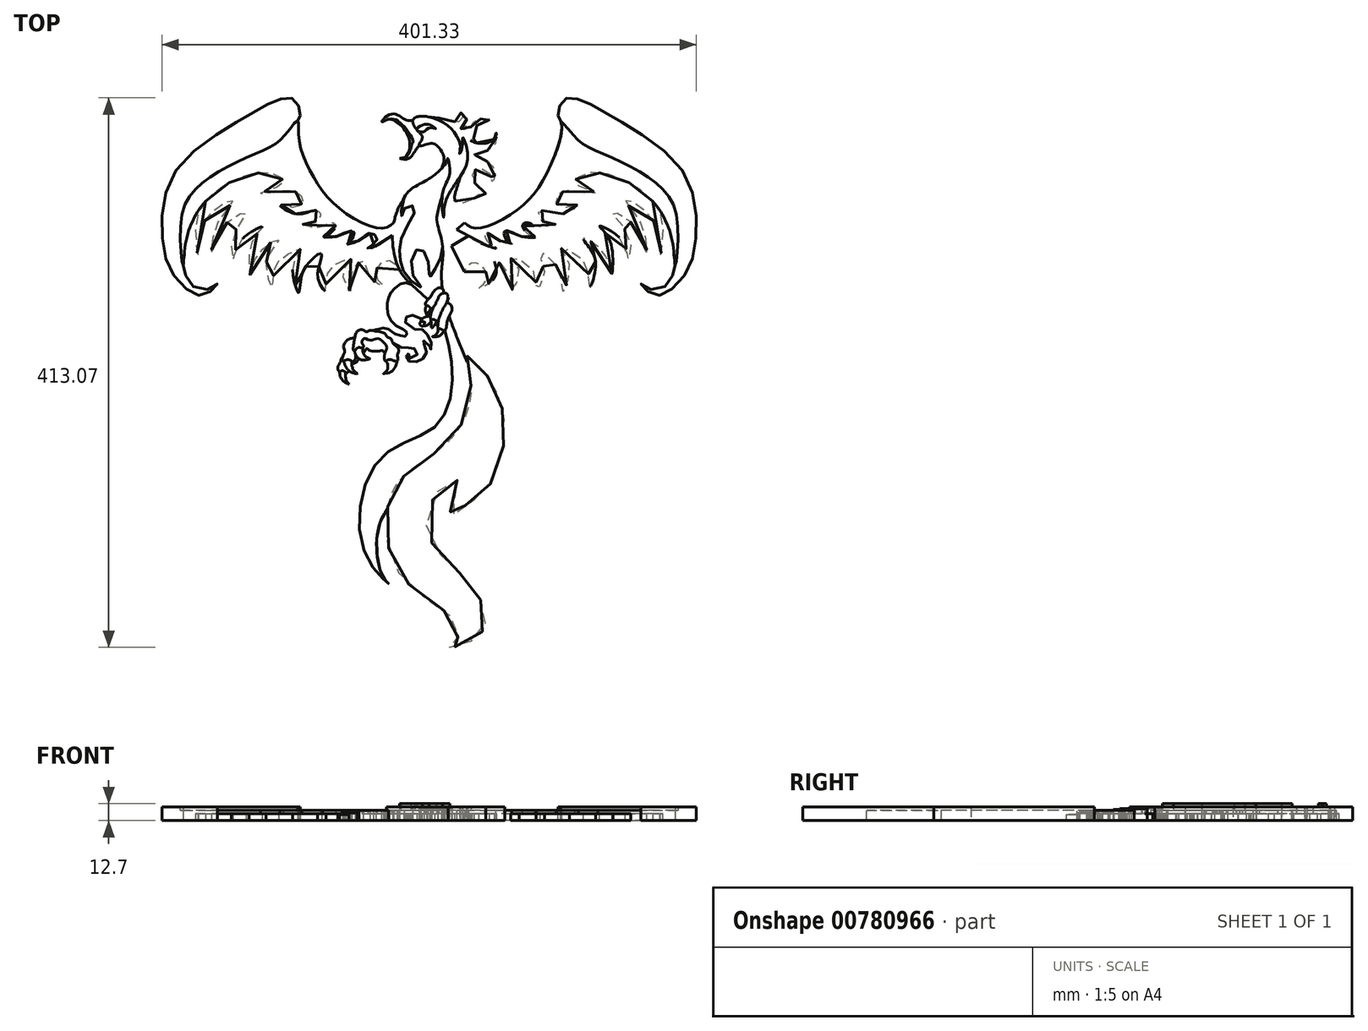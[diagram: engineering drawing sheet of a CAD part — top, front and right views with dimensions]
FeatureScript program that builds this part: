
annotation { "Feature Type Name" : "Feature", "Feature Type Description" : "" }
export const myFeature = defineFeature(function(context is Context, id is Id, definition is map)
    precondition{}
    {
        {
            var Q0;
            Q0=qCreatedBy(makeId("Top.planeOp"),FACE);
            var sketch = newSketch(context, id + "F0", { "sketchPlane" : qUnion([Q0])});
            skFitSpline(sketch, "E0", {"points": [v(-8.67, -5.4) * mm, v(-1.51, -5.23) * mm, v(5.92, 4.18) * mm], "startDerivative": vector(15.7, -3.66) * mm, "endDerivative": vector(12.22, 12.43) * mm});
            skFitSpline(sketch, "E1", {"points": [v(-8.67, -5.4) * mm, v(-2.53, -3.06) * mm, v(0.73, 5.89) * mm, v(1.36, 7.8) * mm, v(-8.37, 21.6) * mm, v(-17.76, 23.8) * mm, v(-21.93, 22.06) * mm, v(-17.64, 26.92) * mm, v(-9.88, 27.16) * mm, v(-3.62, 23.33) * mm, v(1.2, 23.22) * mm], "startDerivative": vector(82.86, 14.8) * mm, "endDerivative": vector(29.37, 4.58) * mm});
            skFitSpline(sketch, "E2", {"points": [v(1.2, 23.22) * mm, v(2.12, 19.15) * mm, v(7.1, 12.99) * mm, v(8.33, 9.8) * mm, v(5.92, 4.18) * mm], "startDerivative": vector(-2.31, -12.7) * mm, "endDerivative": vector(8.26, -4.5) * mm});
            skFitSpline(sketch, "E3", {"points": [v(5.92, 4.18) * mm, v(10.45, 4.85) * mm, v(16.15, 5.81) * mm, v(20.15, 3.52) * mm, v(24.67, -6.53) * mm, v(22.82, -13.16) * mm, v(26.33, -8) * mm, v(27.43, -5.42) * mm, v(28.96, -12.46) * mm, v(28.03, -20.36) * mm, v(23.4, -32.68) * mm, v(24.32, -49.78) * mm, v(25.42, -39.7) * mm, v(36.84, -18.84) * mm, v(42.4, -2.62) * mm, v(38.88, 10.39) * mm, v(38.42, 3.1) * mm, v(36.33, -2.1) * mm, v(36.95, 3.26) * mm, v(32.84, 13.56) * mm, v(26.03, 20.48) * mm, v(12.13, 26.04) * mm, v(3, 25.35) * mm, v(1.2, 23.22) * mm], "startDerivative": vector(43.44, -38.23) * mm, "endDerivative": vector(-67.27, -103.93) * mm});
            skFitSpline(sketch, "E4", {"points": [v(12.13, 26.04) * mm, v(15.22, 26.19) * mm, v(18.86, 25.62) * mm, v(27.7, 22.76) * mm, v(33.96, 22.28) * mm, v(38.93, 24.76) * mm, v(36.9, 29.97) * mm, v(39.54, 27.16) * mm, v(41.95, 23.13) * mm, v(39.78, 17.7) * mm, v(37.35, 16.77) * mm, v(41.25, 16.3) * mm, v(44.74, 17.94) * mm, v(46.59, 21.82) * mm, v(51.24, 24.3) * mm, v(57.52, 23.6) * mm, v(59.02, 24.23) * mm, v(56.82, 22.27) * mm, v(51.47, 21.43) * mm, v(48.3, 16.62) * mm, v(47.68, 11.2) * mm, v(45.76, 8.24) * mm, v(44.62, 8.18) * mm, v(47.37, 6.77) * mm, v(56.63, 6.21) * mm, v(62.77, 10.38) * mm, v(63.86, 13.8) * mm, v(63.97, 8.3) * mm, v(60.46, 2.6) * mm, v(52.02, -1.13) * mm, v(47.62, -2) * mm, v(49.17, -4.1) * mm, v(56.29, -7.21) * mm, v(62.38, -13.48) * mm, v(62.38, -20.12) * mm, v(61, -23.18) * mm, v(59.48, -17.45) * mm, v(49.83, -13.4) * mm, v(45.95, -16.8) * mm, v(47.8, -23.81) * mm, v(52.8, -28.94) * mm, v(56.06, -32.14) * mm, v(52.13, -32.13) * mm, v(43.68, -37.59) * mm, v(32.95, -37.47) * mm, v(36.84, -18.84) * mm], "startDerivative": vector(205.97, 15.52) * mm, "endDerivative": vector(10.23, 256.7) * mm});
            skFitSpline(sketch, "E5", {"points": [v(22.82, -13.16) * mm, v(11.24, -22.05) * mm, v(-5.1, -34.67) * mm, v(-7.41, -48.86) * mm, v(-4.2, -41.9) * mm, v(2.54, -42.64) * mm, v(-6.53, -63.03) * mm, v(-8.4, -80.24) * mm, v(-2.77, -94.45) * mm, v(8.3, -102.75) * mm, v(0.37, -90.76) * mm, v(5.71, -73.25) * mm, v(13.09, -83.94) * mm, v(13.64, -94.45) * mm, v(18.06, -88.18) * mm, v(23.52, -71.72) * mm, v(19.43, -52.46) * mm, v(20.97, -41.44) * mm, v(23.4, -32.68) * mm], "startDerivative": vector(-178.8, -166.71) * mm, "endDerivative": vector(68.52, 243.93) * mm});
            skFitSpline(sketch, "E6", {"points": [v(36.84, -18.84) * mm, v(32.95, -37.47) * mm, v(43.41, -66.2) * mm, v(33.77, -122.4) * mm, v(49.97, -143.97) * mm, v(89.81, -174.41) * mm, v(99.05, -195) * mm, v(91.6, -185.33) * mm, v(69.37, -169.92) * mm, v(96.61, -209.66) * mm, v(65.57, -275.96) * mm, v(59.93, -314.37) * mm, v(73.97, -336.1) * mm, v(54.52, -318.94) * mm, v(41.72, -279.7) * mm, v(61.44, -227.4) * mm, v(47.15, -170.24) * mm, v(23.12, -99.01) * mm], "startDerivative": vector(-182.42, -334.69) * mm, "endDerivative": vector(10.33, 536.26) * mm});
            skFitSpline(sketch, "E7", {"points": [v(-5.1, -34.67) * mm, v(-10.55, -45) * mm, v(-13.94, -60.48) * mm, v(-11.55, -82.2) * mm, v(-3.83, -96.22) * mm, v(10.63, -109.72) * mm, v(20.2, -122.95) * mm, v(30.07, -156.04) * mm, v(20.34, -204.72) * mm, v(-23.05, -230.83) * mm, v(-34.59, -302.46) * mm, v(-17.09, -324.94) * mm, v(-21.5, -318.95) * mm, v(-23.29, -278.8) * mm, v(0, -254.64) * mm, v(24.7, -238.54) * mm, v(40.92, -217.08) * mm, v(47.15, -170.24) * mm, v(23.12, -99.01) * mm, v(23.52, -71.72) * mm], "startDerivative": vector(-275.41, -490.32) * mm, "endDerivative": vector(-88.37, 555.9) * mm});
            skFitSpline(sketch, "E8", {"points": [v(-16.35, 24.17) * mm, v(-13.7, 23.48) * mm, v(-6.2, 17.76) * mm, v(-2.4, 11.42) * mm, v(-1.24, 7.43) * mm, v(-1.17, 2.67) * mm, v(-4.02, -4.31) * mm], "startDerivative": vector(25.5, -4.77) * mm, "endDerivative": vector(-29.98, -38.45) * mm});
            skSolve(sketch);
        }
        {
            var Q0;
            {var subQ2=sQuery(id+"F0.wireOp",EDGE,"E7");Q0=makeQuery(id+"F0.imprint","IMPRINT",FACE,{"disambiguationData":[TD([[makeQuery(id+"F0.imprint","IMPRINT",EDGE,{"derivedFrom":subQ2}),1.0]])]});}
            extrude(context, id + "F1", {"entities" : qUnion([Q0]), "depth" : 7.62 * mm, "offsetDistance" : 25.4 * mm});
        }
        {
            var Q0;
            {var subQ5=sQuery(id+"F0.wireOp",EDGE,"E2");Q0=makeQuery(id+"F0.imprint","IMPRINT",FACE,{"disambiguationData":[TD([[makeQuery(id+"F0.imprint","IMPRINT",EDGE,{"derivedFrom":subQ5}),1.0]])]});}
            extrude(context, id + "F2", {"entities" : qUnion([Q0]), "operationType" : NewBodyOperationType.ADD, "depth" : 10.16 * mm, "offsetDistance" : 25.4 * mm});
        }
        {
            var Q0;
            {var subQ0=sQuery(id+"F0.wireOp",EDGE,"E5");var subQ1=sQuery(id+"F0.wireOp",EDGE,"E3");var subQ2=makeQuery(id+"F0.imprint","INTERSECT",VERTEX,{"disambiguationData":[OD(0.0)],"derivedFrom":[subQ1,subQ0]});Q0=makeQuery(id+"F0.imprint","IMPRINT",FACE,{"disambiguationData":[TD([[makeQuery(id+"F0.imprint","IMPRINT",EDGE,{"disambiguationData":[TD([[subQ2,-1.0]])],"derivedFrom":subQ1}),-1.0]])]});}
            extrude(context, id + "F3", {"entities" : qUnion([Q0]), "operationType" : NewBodyOperationType.ADD, "depth" : 12.7 * mm, "offsetDistance" : 25.4 * mm});
        }
        {
            var Q0;
            {var subQ0=sQuery(id+"F0.wireOp",EDGE,"E4");Q0=makeQuery(id+"F0.imprint","IMPRINT",FACE,{"disambiguationData":[TD([[makeQuery(id+"F0.imprint","IMPRINT",EDGE,{"derivedFrom":subQ0}),-1.0]])]});}
            extrude(context, id + "F4", {"entities" : qUnion([Q0]), "operationType" : NewBodyOperationType.ADD, "depth" : 5.08 * mm, "offsetDistance" : 25.4 * mm});
        }
        {
            var Q0;
            Q0=makeQuery(id+"F0.imprint","IMPRINT",FACE,{"disambiguationData":[TD([[makeQuery(id+"F0.imprint","IMPRINT",EDGE,{"derivedFrom":sQuery(id+"F0.wireOp",EDGE,"E0")}),1.0]])]});
            extrude(context, id + "F5", {"entities" : qUnion([Q0]), "operationType" : NewBodyOperationType.ADD, "depth" : 7.62 * mm, "offsetDistance" : 25.4 * mm});
        }
        {
            var Q0;
            {var subQ0=sQuery(id+"F0.wireOp",EDGE,"E8");Q0=makeQuery(id+"F0.imprint","IMPRINT",FACE,{"disambiguationData":[TD([[makeQuery(id+"F0.imprint","IMPRINT",EDGE,{"derivedFrom":subQ0}),1.0]])]});}
            extrude(context, id + "F6", {"entities" : qUnion([Q0]), "operationType" : NewBodyOperationType.ADD, "depth" : 5.08 * mm, "offsetDistance" : 25.4 * mm});
        }
        {
            var Q0;
            Q0=qCreatedBy(makeId("Top.planeOp"),FACE);
            var sketch = newSketch(context, id + "F7", { "sketchPlane" : qUnion([Q0])});
            skFitSpline(sketch, "E9", {"points": [v(-0.05, -100.04) * mm, v(-7, -99.44) * mm, v(-15.14, -106.14) * mm, v(-17.67, -112.32) * mm, v(-17.85, -120.4) * mm, v(-12.81, -129.85) * mm, v(-4, -135.24) * mm, v(-3.6, -136.14) * mm, v(-3.7, -138.8) * mm, v(-7, -138.9) * mm, v(-13.37, -136.6) * mm, v(-15.47, -134.55) * mm, v(-22.15, -132.9) * mm, v(-23.45, -133.48) * mm, v(-24.06, -133.81) * mm, v(-24.8, -133.81) * mm, v(-27.03, -134.13) * mm, v(-28.4, -134.86) * mm, v(-25.76, -135.3) * mm, v(-19.62, -137.13) * mm, v(-18.12, -139.43) * mm, v(-15.05, -141.02) * mm, v(-13.85, -143.78) * mm, v(-4.3, -147.98) * mm, v(-1.16, -147.63) * mm, v(3.71, -149.11) * mm, v(3.4, -154.42) * mm, v(-2.96, -154.63) * mm, v(-1.88, -151.62) * mm, v(-4.02, -154.84) * mm, v(-0.49, -158.24) * mm, v(5.25, -157.93) * mm, v(9.91, -154.71) * mm, v(11.49, -148.47) * mm, v(8.27, -142.42) * mm, v(13.31, -145) * mm, v(14.62, -149.47) * mm, v(15.27, -146.9) * mm, v(14.15, -141.1) * mm, v(8.44, -133.89) * mm, v(5.23, -134.6) * mm, v(-5.18, -127.03) * mm, v(-2.66, -124.12) * mm, v(2.14, -123.44) * mm, v(14.91, -129.74) * mm, v(20.87, -129.74) * mm, v(23.08, -129.18) * mm], "startDerivative": vector(-259.15, 144.37) * mm, "endDerivative": vector(81.22, 23.95) * mm});
            skFitSpline(sketch, "E10", {"points": [v(-28.4, -134.86) * mm, v(-29.8, -134.86) * mm, v(-31.04, -134.63) * mm, v(-33.06, -135.6) * mm, v(-36.37, -134.38) * mm, v(-40.34, -135.1) * mm, v(-42.2, -139.48) * mm, v(-43.05, -143.55) * mm, v(-43.4, -146.9) * mm, v(-43.6, -148.85) * mm, v(-42.73, -150.17) * mm, v(-40, -147.63) * mm, v(-36.53, -147.75) * mm, v(-35.76, -146.13) * mm, v(-36.92, -144.07) * mm, v(-35.42, -140.74) * mm, v(-30.25, -142.24) * mm, v(-25.82, -140.8) * mm, v(-20.08, -144.12) * mm, v(-18.28, -148.03) * mm, v(-20.02, -152.96) * mm, v(-19.4, -157.7) * mm, v(-17.45, -156.72) * mm, v(-14.15, -156.98) * mm, v(-10.5, -157.7) * mm, v(-9.9, -155.4) * mm, v(-10.28, -152.79) * mm, v(-9.3, -149.86) * mm, v(-10.05, -147.7) * mm, v(-11.29, -146.54) * mm, v(-12.24, -145.65) * mm, v(-13.85, -143.78) * mm], "startDerivative": vector(-126.28, 25.7) * mm, "endDerivative": vector(-46.26, 137.95) * mm});
            skFitSpline(sketch, "E11", {"points": [v(-42.2, -139.48) * mm, v(-45.85, -140.83) * mm, v(-48.34, -142.22) * mm, v(-50.14, -144.52) * mm, v(-50.85, -147.35) * mm, v(-49.91, -150.65) * mm, v(-50.5, -152.34) * mm, v(-51.66, -155.06) * mm, v(-51.3, -157.56) * mm, v(-48.67, -156.8) * mm, v(-45.55, -157.16) * mm, v(-44.27, -158.06) * mm, v(-42.54, -157.28) * mm, v(-41.75, -154.38) * mm, v(-41.87, -152.53) * mm], "startDerivative": vector(-26.53, -31.12) * mm, "endDerivative": vector(-3.12, 47.85) * mm});
            skFitSpline(sketch, "E12", {"points": [v(-19.4, -157.7) * mm, v(-18.01, -159.15) * mm, v(-17.67, -162.54) * mm, v(-18.37, -165.08) * mm, v(-20.85, -167.18) * mm, v(-18.45, -166.8) * mm, v(-15, -165.68) * mm, v(-12, -162.16) * mm, v(-11.03, -159.08) * mm, v(-10.5, -157.7) * mm], "startDerivative": vector(17.76, -12.44) * mm, "endDerivative": vector(6.99, 15.7) * mm});
            skFitSpline(sketch, "E13", {"points": [v(-42.73, -150.17) * mm, v(-41.87, -152.53) * mm, v(-39.64, -155.63) * mm, v(-36.35, -156.92) * mm, v(-32.38, -156.48) * mm, v(-31.05, -155.87) * mm, v(-32.09, -155.45) * mm, v(-34.15, -154.43) * mm, v(-35.7, -152.12) * mm, v(-36.34, -150.17) * mm, v(-36.53, -147.75) * mm], "startDerivative": vector(15.67, -24.18) * mm, "endDerivative": vector(-3.95, 15.32) * mm});
            skFitSpline(sketch, "E14", {"points": [v(-51.3, -157.56) * mm, v(-50.16, -159.43) * mm, v(-49.26, -161.63) * mm, v(-48.22, -163.28) * mm, v(-46.96, -164.92) * mm, v(-45.42, -165.93) * mm, v(-42.58, -166.92) * mm, v(-40.6, -167.2) * mm, v(-42.51, -165.5) * mm, v(-44, -163.01) * mm, v(-44.68, -159.78) * mm, v(-44.27, -158.06) * mm], "startDerivative": vector(27.67, -20.95) * mm, "endDerivative": vector(13.92, 15.87) * mm});
            skFitSpline(sketch, "E15", {"points": [v(-51.66, -155.06) * mm, v(-52.8, -157.14) * mm, v(-54.13, -160.22) * mm, v(-55.19, -162.65) * mm, v(-54.6, -164.83) * mm, v(-53.92, -165.57) * mm, v(-52.22, -165.04) * mm, v(-50.2, -165.46) * mm, v(-48.99, -166.47) * mm, v(-47.88, -166.36) * mm, v(-46.96, -164.92) * mm], "startDerivative": vector(-25.42, -13.3) * mm, "endDerivative": vector(3.8, 21.11) * mm});
            skFitSpline(sketch, "E16", {"points": [v(-53.92, -165.57) * mm, v(-53.65, -167.48) * mm, v(-53.33, -169.28) * mm, v(-52.38, -171.03) * mm, v(-51, -172.57) * mm, v(-48.78, -174.2) * mm, v(-46.88, -175) * mm, v(-48.09, -173.41) * mm, v(-48.99, -171.45) * mm, v(-49.3, -169.33) * mm, v(-49.3, -167.58) * mm, v(-48.99, -166.47) * mm], "startDerivative": vector(7.77, -26.41) * mm, "endDerivative": vector(13.13, 12.03) * mm});
            skFitSpline(sketch, "E17", {"points": [v(-44.68, -159.78) * mm, v(-43.41, -159.53) * mm, v(-42.06, -159.18) * mm, v(-40.86, -158.2) * mm, v(-40.01, -156.9) * mm, v(-40.1, -155.2) * mm], "startDerivative": vector(13.67, 4.14) * mm, "endDerivative": vector(0.69, 4.69) * mm});
            skFitSpline(sketch, "E18", {"points": [v(-35.98, -151.52) * mm, v(-34.9, -150.38) * mm, v(-33.29, -148.2) * mm, v(-32.1, -149.37) * mm, v(-28.9, -150.26) * mm, v(-26.32, -150.41) * mm, v(-23.49, -150.04) * mm, v(-21.6, -149.76) * mm, v(-20.69, -150.68) * mm, v(-19.73, -151.92) * mm], "startDerivative": vector(8.82, 8.41) * mm, "endDerivative": vector(10.7, -12.63) * mm});
            skLineSegment(sketch, "E19", {"start": v(-0.05, -100.04) * mm, "end": v(28.04, -110.01) * mm});
            skLineSegment(sketch, "E20", {"start": v(28.04, -110.01) * mm, "end": v(23.08, -129.18) * mm});
            skSolve(sketch);
        }
        {
            var Q0;
            {var subQ0=sQuery(id+"F7.wireOp",EDGE,"E19");Q0=makeQuery(id+"F7.imprint","IMPRINT",FACE,{"disambiguationData":[TD([[makeQuery(id+"F7.imprint","IMPRINT",EDGE,{"derivedFrom":subQ0}),-1.0]])]});}
            extrude(context, id + "F8", {"entities" : qUnion([Q0]), "operationType" : NewBodyOperationType.ADD, "depth" : 5.08 * mm, "offsetDistance" : 25.4 * mm});
        }
        {
            var Q0;
            {var subQ1=sQuery(id+"F7.wireOp",EDGE,"E10");var subQ5=sQuery(id+"F7.wireOp",EDGE,"E9");var subQ6=makeQuery(id+"F7.imprint","INTERSECT",VERTEX,{"disambiguationData":[OD(0.0)],"derivedFrom":[subQ5,subQ1]});Q0=makeQuery(id+"F7.imprint","IMPRINT",FACE,{"disambiguationData":[TD([[makeQuery(id+"F7.imprint","IMPRINT",EDGE,{"disambiguationData":[TD([[subQ6,-1.0]])],"derivedFrom":subQ5}),-1.0]])]});}
            extrude(context, id + "F9", {"entities" : qUnion([Q0]), "operationType" : NewBodyOperationType.ADD, "depth" : 7.62 * mm, "offsetDistance" : 25.4 * mm});
        }
        {
            var Q0;
            {var subQ1=sQuery(id+"F7.wireOp",EDGE,"E11");var subQ5=sQuery(id+"F7.wireOp",EDGE,"E10");var subQ6=makeQuery(id+"F7.imprint","INTERSECT",VERTEX,{"derivedFrom":[subQ5,subQ1]});Q0=makeQuery(id+"F7.imprint","IMPRINT",FACE,{"disambiguationData":[TD([[makeQuery(id+"F7.imprint","IMPRINT",EDGE,{"disambiguationData":[TD([[subQ6,-1.0]])],"derivedFrom":subQ5}),-1.0]])]});}
            extrude(context, id + "F10", {"entities" : qUnion([Q0]), "operationType" : NewBodyOperationType.ADD, "depth" : 6.35 * mm, "offsetDistance" : 25.4 * mm});
        }
        {
            var Q0;
            {var subQ3=sQuery(id+"F7.wireOp",EDGE,"E18");Q0=makeQuery(id+"F7.imprint","IMPRINT",FACE,{"disambiguationData":[TD([[makeQuery(id+"F7.imprint","IMPRINT",EDGE,{"derivedFrom":subQ3}),1.0]])]});}
            var Q1;
            {var subQ5=sQuery(id+"F7.wireOp",EDGE,"E17");Q1=makeQuery(id+"F7.imprint","IMPRINT",FACE,{"disambiguationData":[TD([[makeQuery(id+"F7.imprint","IMPRINT",EDGE,{"derivedFrom":subQ5}),1.0]])]});}
            var Q2;
            {var subQ4=sQuery(id+"F7.wireOp",EDGE,"E11");var subQ6=sQuery(id+"F7.wireOp",EDGE,"E14");var subQ7=makeQuery(id+"F7.imprint","INTERSECT",VERTEX,{"disambiguationData":[OD(0.0)],"derivedFrom":[subQ4,subQ6]});Q2=makeQuery(id+"F7.imprint","IMPRINT",FACE,{"disambiguationData":[TD([[makeQuery(id+"F7.imprint","IMPRINT",EDGE,{"disambiguationData":[TD([[subQ7,1.0]])],"derivedFrom":subQ4}),-1.0]])]});}
            extrude(context, id + "F11", {"entities" : qUnion([Q0, Q1, Q2]), "operationType" : NewBodyOperationType.ADD, "depth" : 5.08 * mm, "offsetDistance" : 25.4 * mm});
        }
        {
            var Q0;
            {var subQ0=sQuery(id+"F7.wireOp",EDGE,"E16");Q0=makeQuery(id+"F7.imprint","IMPRINT",FACE,{"disambiguationData":[TD([[makeQuery(id+"F7.imprint","IMPRINT",EDGE,{"derivedFrom":subQ0}),1.0]])]});}
            extrude(context, id + "F12", {"entities" : qUnion([Q0]), "operationType" : NewBodyOperationType.ADD, "depth" : 4.44 * mm, "offsetDistance" : 25.4 * mm});
        }
        {
            var Q0;
            {var subQ0=sQuery(id+"F7.wireOp",EDGE,"E14");var subQ1=sQuery(id+"F7.wireOp",EDGE,"E11");var subQ2=makeQuery(id+"F7.imprint","INTERSECT",VERTEX,{"disambiguationData":[OD(0.0)],"derivedFrom":[subQ1,subQ0]});Q0=makeQuery(id+"F7.imprint","IMPRINT",FACE,{"disambiguationData":[TD([[makeQuery(id+"F7.imprint","IMPRINT",EDGE,{"disambiguationData":[TD([[subQ2,-1.0]])],"derivedFrom":subQ1}),-1.0]])]});}
            extrude(context, id + "F13", {"entities" : qUnion([Q0]), "operationType" : NewBodyOperationType.ADD, "depth" : 5.7 * mm, "offsetDistance" : 25.4 * mm});
        }
        {
            var Q0;
            {var subQ0=sQuery(id+"F7.wireOp",EDGE,"E13");var subQ4=sQuery(id+"F7.wireOp",EDGE,"E10");var subQ5=makeQuery(id+"F7.imprint","INTERSECT",VERTEX,{"disambiguationData":[OD(0.0)],"derivedFrom":[subQ4,subQ0]});Q0=makeQuery(id+"F7.imprint","IMPRINT",FACE,{"disambiguationData":[TD([[makeQuery(id+"F7.imprint","IMPRINT",EDGE,{"disambiguationData":[TD([[subQ5,-1.0]])],"derivedFrom":subQ4}),-1.0]])]});}
            var Q1;
            {var subQ0=sQuery(id+"F7.wireOp",EDGE,"E12");Q1=makeQuery(id+"F7.imprint","IMPRINT",FACE,{"disambiguationData":[TD([[makeQuery(id+"F7.imprint","IMPRINT",EDGE,{"derivedFrom":subQ0}),1.0]])]});}
            extrude(context, id + "F14", {"entities" : qUnion([Q0, Q1]), "operationType" : NewBodyOperationType.ADD, "depth" : 7 * mm, "offsetDistance" : 25.4 * mm});
        }
        {
            var Q0;
            Q0=qCreatedBy(makeId("Top.planeOp"),FACE);
            var sketch = newSketch(context, id + "F15", { "sketchPlane" : qUnion([Q0])});
            skFitSpline(sketch, "E21", {"points": [v(40.02, -53.8) * mm, v(48.94, -57.92) * mm, v(78.57, -44.94) * mm, v(101.16, -17.9) * mm, v(113.1, 18.52) * mm, v(112.35, 22.9) * mm, v(121.04, 13) * mm, v(131.84, 3.6) * mm, v(155.22, -6.78) * mm, v(185.2, -25.07) * mm, v(199.9, -52.06) * mm, v(198.4, -85.64) * mm, v(196.3, -68.55) * mm, v(181.6, -37.67) * mm, v(157.59, -20.7) * mm, v(131.02, -16.77) * mm, v(123.6, -24.26) * mm, v(140.03, -31.4) * mm, v(127.9, -30.32) * mm, v(114.08, -30.32) * mm, v(108.54, -35.67) * mm, v(112.93, -42.12) * mm, v(125.48, -40.4) * mm, v(113.77, -47.08) * mm, v(98.99, -44.59) * mm, v(95, -47.44) * mm, v(101.79, -54.1) * mm, v(109.2, -54.41) * mm, v(97.44, -57.17) * mm, v(88.43, -53.99) * mm, v(83.96, -54.93) * mm, v(87.16, -61.52) * mm, v(93.36, -64.55) * mm, v(85.42, -64.55) * mm, v(78.36, -62.06) * mm, v(70.36, -60.2) * mm, v(71.57, -66.52) * mm, v(75.39, -69.91) * mm, v(66.9, -67.58) * mm, v(62, -63.65) * mm, v(56.15, -61.87) * mm, v(56.9, -67.23) * mm, v(63.63, -72.92) * mm, v(55.58, -70.38) * mm, v(43.1, -63.53) * mm], "startDerivative": vector(375.92, -335.18) * mm, "endDerivative": vector(-175.71, 347.77) * mm});
            skFitSpline(sketch, "E22", {"points": [v(181.6, -37.67) * mm, v(188.96, -55.1) * mm, v(187.01, -79.15) * mm, v(186.76, -66.55) * mm, v(176.23, -45.37) * mm, v(161.11, -36.35) * mm, v(165.38, -43.8) * mm, v(175.33, -61.2) * mm, v(176.58, -76.53) * mm, v(173, -65.8) * mm, v(161.36, -50.41) * mm, v(150.9, -46.05) * mm, v(164.1, -65.12) * mm, v(162.85, -81.35) * mm, v(159.82, -69.23) * mm, v(141.64, -56.21) * mm, v(146.63, -62.63) * mm, v(151.5, -80) * mm, v(150.73, -92.05) * mm, v(149.1, -85.85) * mm, v(138.9, -70.73) * mm, v(129.34, -65.66) * mm, v(135.22, -74.4) * mm, v(138.43, -88.12) * mm, v(134.35, -101.64) * mm, v(132.92, -90.6) * mm, v(126.62, -79.66) * mm, v(113.13, -72.91) * mm, v(116.44, -79.8) * mm, v(118.69, -90.9) * mm, v(114.32, -105.77) * mm, v(112.54, -95.43) * mm, v(105.94, -82.24) * mm, v(97.38, -76.13) * mm, v(98, -82.8) * mm, v(99.77, -94.03) * mm, v(94.35, -104.37) * mm, v(93.72, -96.8) * mm, v(87.17, -84.45) * mm, v(75.07, -80.3) * mm, v(79.63, -86.14) * mm, v(80.05, -96.52) * mm, v(75.07, -104.8) * mm, v(75.39, -97.48) * mm, v(67.97, -85.18) * mm, v(62.66, -82.1) * mm, v(63.97, -88.93) * mm, v(58.88, -99.21) * mm, v(50.94, -103.02) * mm, v(54.54, -99.52) * mm, v(55.8, -90.1) * mm, v(47.94, -83.87) * mm, v(42.46, -86.47) * mm, v(39.9, -90.65) * mm], "startDerivative": vector(450.46, -609.8) * mm, "endDerivative": vector(-134.4, -506.85) * mm});
            skLineSegment(sketch, "E23", {"start": v(-13.05, -53.8) * mm, "end": v(40.02, -53.8) * mm, "construction": true});
            skPoint(sketch, "E24", {"position": v(13.48, -53.8) * mm});
            skLineSegment(sketch, "E25", {"start": v(13.48, 55.97) * mm, "end": v(13.48, -132.3) * mm, "construction": true});
            skFitSpline(sketch, "E26", {"points": [v(112.35, 22.9) * mm, v(110.51, 24.98) * mm, v(110.51, 29.93) * mm, v(114.26, 38.47) * mm, v(122.36, 39.82) * mm, v(137.65, 33.68) * mm, v(161.79, 19.73) * mm, v(204.51, -15.65) * mm, v(214.08, -59.05) * mm, v(207.03, -90.67) * mm, v(189.96, -107.17) * mm, v(179.34, -106.59) * mm, v(172.7, -99.64) * mm, v(184.3, -104.72) * mm, v(195.87, -94.25) * mm, v(198.4, -85.64) * mm], "startDerivative": vector(-78.32, 64.82) * mm, "endDerivative": vector(78.22, 286.12) * mm});
            skFitSpline(sketch, "E27.MirrorCS", {"points": [v(-13.05, -53.8) * mm, v(-21.97, -57.92) * mm, v(-51.6, -44.94) * mm, v(-74.2, -17.9) * mm, v(-84.48, 10.9) * mm, v(-85.38, 22.9) * mm, v(-94.07, 13) * mm, v(-104.87, 3.6) * mm, v(-128.26, -6.78) * mm, v(-158.24, -25.07) * mm, v(-172.93, -52.06) * mm, v(-171.43, -85.64) * mm, v(-169.33, -68.55) * mm, v(-154.62, -37.67) * mm, v(-130.62, -20.7) * mm, v(-104.05, -16.77) * mm, v(-96.62, -24.26) * mm, v(-113.06, -31.4) * mm, v(-100.93, -30.32) * mm, v(-87.11, -30.32) * mm, v(-81.57, -35.67) * mm, v(-85.96, -42.12) * mm, v(-98.52, -40.4) * mm, v(-86.8, -47.08) * mm, v(-72.02, -44.59) * mm, v(-68.03, -47.44) * mm, v(-74.82, -54.1) * mm, v(-82.24, -54.41) * mm, v(-70.47, -57.17) * mm, v(-61.46, -53.99) * mm, v(-57, -54.93) * mm, v(-60.2, -61.52) * mm, v(-66.4, -64.55) * mm, v(-58.46, -64.55) * mm, v(-51.4, -62.06) * mm, v(-43.39, -60.2) * mm, v(-44.6, -66.52) * mm, v(-48.42, -69.91) * mm, v(-39.94, -67.58) * mm, v(-35.03, -63.65) * mm, v(-29.18, -61.87) * mm, v(-25.88, -67.23) * mm, v(-32.62, -72.92) * mm, v(-24.56, -70.38) * mm, v(-14.07, -63.26) * mm], "startDerivative": vector(-375.92, -335.18) * mm, "endDerivative": vector(421.18, 165.87) * mm});
            skFitSpline(sketch, "E28.MirrorCS", {"points": [v(-154.62, -37.67) * mm, v(-162, -55.1) * mm, v(-160.04, -79.15) * mm, v(-159.8, -66.55) * mm, v(-149.26, -45.37) * mm, v(-134.14, -36.35) * mm, v(-138.41, -43.8) * mm, v(-148.37, -61.2) * mm, v(-149.61, -76.53) * mm, v(-146.02, -65.8) * mm, v(-134.39, -50.41) * mm, v(-123.94, -46.05) * mm, v(-134.43, -65.87) * mm, v(-133.19, -82.1) * mm, v(-130.16, -69.97) * mm, v(-111.97, -56.96) * mm, v(-116.96, -63.38) * mm, v(-121.83, -80.76) * mm, v(-121.06, -92.8) * mm, v(-119.42, -86.6) * mm, v(-109.24, -71.48) * mm, v(-99.67, -66.4) * mm, v(-105.55, -75.15) * mm, v(-108.76, -88.87) * mm, v(-104.68, -102.4) * mm, v(-103.25, -91.35) * mm, v(-96.95, -80.4) * mm, v(-83.46, -73.66) * mm, v(-86.77, -80.56) * mm, v(-89.02, -91.65) * mm, v(-84.65, -106.52) * mm, v(-82.87, -96.18) * mm, v(-76.27, -82.99) * mm, v(-67.71, -76.88) * mm, v(-68.34, -83.56) * mm, v(-70.1, -94.78) * mm, v(-64.68, -105.12) * mm, v(-64.05, -97.55) * mm, v(-57.5, -85.2) * mm, v(-45.4, -81.05) * mm, v(-49.96, -86.89) * mm, v(-50.38, -97.27) * mm, v(-45.4, -105.54) * mm, v(-45.72, -98.23) * mm, v(-41, -85.18) * mm, v(-35.7, -82.1) * mm, v(-33.93, -86.92) * mm, v(-28.84, -97.2) * mm, v(-20.9, -101) * mm, v(-24.5, -97.5) * mm, v(-25.76, -88.08) * mm, v(-17.9, -81.86) * mm, v(-12.42, -84.46) * mm, v(-8.79, -89.13) * mm], "startDerivative": vector(-450.46, -609.8) * mm, "endDerivative": vector(294, -556.93) * mm});
            skFitSpline(sketch, "E29.MirrorCS", {"points": [v(-85.38, 22.9) * mm, v(-83.55, 24.98) * mm, v(-83.55, 29.93) * mm, v(-87.3, 38.47) * mm, v(-95.39, 39.82) * mm, v(-110.68, 33.68) * mm, v(-134.82, 19.73) * mm, v(-177.55, -15.65) * mm, v(-187.1, -59.05) * mm, v(-180.06, -90.67) * mm, v(-163, -107.17) * mm, v(-152.37, -106.59) * mm, v(-145.74, -99.64) * mm, v(-157.33, -104.72) * mm, v(-168.9, -94.25) * mm, v(-171.43, -85.64) * mm], "startDerivative": vector(78.32, 64.82) * mm, "endDerivative": vector(-78.22, 286.12) * mm});
            skLineSegment(sketch, "E30", {"start": v(-13.05, -53.8) * mm, "end": v(-8.06, -59.46) * mm});
            skLineSegment(sketch, "E31", {"start": v(-8.06, -59.46) * mm, "end": v(-14.07, -63.26) * mm});
            skLineSegment(sketch, "E32", {"start": v(-14.07, -63.26) * mm, "end": v(-1.64, -76.79) * mm});
            skLineSegment(sketch, "E33", {"start": v(-1.64, -76.79) * mm, "end": v(-8.79, -89.13) * mm});
            skLineSegment(sketch, "E34", {"start": v(40.02, -53.8) * mm, "end": v(34.02, -58.85) * mm});
            skLineSegment(sketch, "E35", {"start": v(34.02, -58.85) * mm, "end": v(43.1, -63.53) * mm});
            skLineSegment(sketch, "E36", {"start": v(39.9, -90.65) * mm, "end": v(30.31, -71.1) * mm});
            skLineSegment(sketch, "E37", {"start": v(30.31, -71.1) * mm, "end": v(43.1, -63.53) * mm});
            skSolve(sketch);
        }
        {
            var Q0;
            {var subQ2=sQuery(id+"F15.wireOp",EDGE,"E22");Q0=makeQuery(id+"F15.imprint","IMPRINT",FACE,{"disambiguationData":[TD([[makeQuery(id+"F15.imprint","IMPRINT",EDGE,{"derivedFrom":subQ2}),-1.0]])]});}
            var Q1;
            {var subQ2=sQuery(id+"F15.wireOp",EDGE,"E28.MirrorCS");Q1=makeQuery(id+"F15.imprint","IMPRINT",FACE,{"disambiguationData":[TD([[makeQuery(id+"F15.imprint","IMPRINT",EDGE,{"derivedFrom":subQ2}),1.0]])]});}
            extrude(context, id + "F16", {"entities" : qUnion([Q0, Q1]), "operationType" : NewBodyOperationType.ADD, "depth" : 5.08 * mm, "offsetDistance" : 25.4 * mm});
        }
        {
            var Q0;
            {var subQ6=sQuery(id+"F15.wireOp",EDGE,"E30");Q0=makeQuery(id+"F15.imprint","IMPRINT",FACE,{"disambiguationData":[TD([[makeQuery(id+"F15.imprint","IMPRINT",EDGE,{"derivedFrom":subQ6}),-1.0]])]});}
            var Q1;
            {var subQ6=sQuery(id+"F15.wireOp",EDGE,"E34");Q1=makeQuery(id+"F15.imprint","IMPRINT",FACE,{"disambiguationData":[TD([[makeQuery(id+"F15.imprint","IMPRINT",EDGE,{"derivedFrom":subQ6}),1.0]])]});}
            extrude(context, id + "F17", {"entities" : qUnion([Q0, Q1]), "operationType" : NewBodyOperationType.ADD, "depth" : 7.62 * mm, "offsetDistance" : 25.4 * mm});
        }
        {
            var Q0;
            {var subQ0=sQuery(id+"F15.wireOp",EDGE,"E26");Q0=makeQuery(id+"F15.imprint","IMPRINT",FACE,{"disambiguationData":[TD([[makeQuery(id+"F15.imprint","IMPRINT",EDGE,{"derivedFrom":subQ0}),-1.0]])]});}
            var Q1;
            {var subQ0=sQuery(id+"F15.wireOp",EDGE,"E29.MirrorCS");Q1=makeQuery(id+"F15.imprint","IMPRINT",FACE,{"disambiguationData":[TD([[makeQuery(id+"F15.imprint","IMPRINT",EDGE,{"derivedFrom":subQ0}),1.0]])]});}
            extrude(context, id + "F18", {"entities" : qUnion([Q0, Q1]), "operationType" : NewBodyOperationType.ADD, "depth" : 10.16 * mm, "offsetDistance" : 25.4 * mm});
        }
        {
            var Q0;
            Q0=qCreatedBy(makeId("Top.planeOp"),FACE);
            var sketch = newSketch(context, id + "F19", { "sketchPlane" : qUnion([Q0])});
            skFitSpline(sketch, "E38", {"points": [v(17.22, -126.6) * mm, v(14.83, -126.26) * mm, v(15.82, -119.5) * mm, v(19.23, -112.82) * mm, v(22.31, -107.52) * mm, v(26.7, -107.08) * mm, v(27.1, -112.68) * mm, v(22.71, -120.8) * mm, v(19.66, -127.44) * mm, v(17.22, -126.6) * mm]});
            skFitSpline(sketch, "E39", {"points": [v(16.49, -117.98) * mm, v(15.03, -118.26) * mm, v(13.66, -116.87) * mm, v(12.25, -116.12) * mm, v(11.4, -116.09) * mm, v(10.76, -114.28) * mm, v(14.43, -109.45) * mm, v(17.63, -104.6) * mm, v(21.19, -102.73) * mm, v(23.46, -103.51) * mm, v(24.42, -105.02) * mm, v(24.76, -106.58) * mm], "startDerivative": vector(-15.29, -6.12) * mm, "endDerivative": vector(15.9, -33.12) * mm});
            skFitSpline(sketch, "E40", {"points": [v(20.64, -126.23) * mm, v(19.98, -131.68) * mm, v(20.05, -132.5) * mm, v(20.3, -133.55) * mm, v(21.84, -133.55) * mm, v(23.74, -134.5) * mm, v(24.85, -134.8) * mm, v(26.17, -133.32) * mm, v(26.92, -128.86) * mm, v(27.54, -126.24) * mm, v(29.68, -121.75) * mm, v(30.78, -117.9) * mm, v(29.62, -115.4) * mm, v(27.75, -114.15) * mm, v(26.34, -114.44) * mm], "startDerivative": vector(-5.14, -26.3) * mm, "endDerivative": vector(-21.48, -15.59) * mm});
            skFitSpline(sketch, "E41", {"points": [v(11.4, -116.09) * mm, v(10.98, -117.46) * mm, v(10.6, -119.24) * mm, v(11.04, -121.3) * mm, v(12.43, -123.93) * mm, v(12.54, -123) * mm, v(13.18, -121) * mm, v(13.88, -119.74) * mm, v(15.03, -118.26) * mm], "startDerivative": vector(-3.88, -11.13) * mm, "endDerivative": vector(9.93, 7.22) * mm});
            skFitSpline(sketch, "E42", {"points": [v(14.83, -126.26) * mm, v(14.9, -127.92) * mm, v(15.01, -129.13) * mm, v(15.11, -130.4) * mm, v(15.18, -131.86) * mm, v(15.51, -132.84) * mm, v(16.11, -132.5) * mm, v(16.76, -131.68) * mm, v(17.38, -130.77) * mm, v(18.05, -129.72) * mm, v(18.43, -129.12) * mm, v(19.66, -127.44) * mm], "startDerivative": vector(-1, -18.53) * mm, "endDerivative": vector(12.74, 19.46) * mm});
            skFitSpline(sketch, "E43", {"points": [v(24.85, -134.8) * mm, v(24.02, -136.13) * mm, v(22.96, -137.46) * mm, v(21.44, -138.49) * mm, v(20.2, -139.1) * mm, v(18.55, -139.43) * mm, v(15.87, -139.43) * mm, v(17.28, -138.86) * mm, v(18.64, -137.81) * mm, v(19.43, -136.63) * mm, v(19.95, -135.52) * mm, v(20.3, -133.55) * mm], "startDerivative": vector(-14.2, -13.25) * mm, "endDerivative": vector(0.22, 18.97) * mm});
            skFitSpline(sketch, "E44", {"points": [v(14.83, -122.65) * mm, v(13.62, -123.7) * mm, v(12.2, -124.15) * mm, v(9.7, -124.97) * mm, v(7.92, -126.3) * mm, v(7.23, -127.94) * mm, v(8.14, -128.18) * mm, v(10.14, -128.46) * mm, v(9.8, -129.99) * mm, v(9.77, -130.97) * mm, v(10.84, -131.1) * mm, v(12.29, -130.72) * mm, v(13.23, -129.9) * mm, v(13.87, -129.04) * mm, v(14.95, -128.39) * mm], "startDerivative": vector(-23.27, -1) * mm, "endDerivative": vector(23.2, 4.9) * mm});
            skFitSpline(sketch, "E45", {"points": [v(7.23, -127.94) * mm, v(6.64, -128.86) * mm, v(6.66, -130.21) * mm, v(7.6, -131.24) * mm, v(8.67, -131.48) * mm, v(9.77, -130.97) * mm], "startDerivative": vector(-3.7, -4.43) * mm, "endDerivative": vector(5.04, 3.5) * mm});
            skSolve(sketch);
        }
        {
            var Q0;
            {var subQ4=sQuery(id+"F19.wireOp",EDGE,"E38");var subQ6=sQuery(id+"F19.wireOp",EDGE,"E42");var subQ7=makeQuery(id+"F19.imprint","INTERSECT",VERTEX,{"disambiguationData":[OD(0.0)],"derivedFrom":[subQ4,subQ6]});Q0=makeQuery(id+"F19.imprint","IMPRINT",FACE,{"disambiguationData":[TD([[makeQuery(id+"F19.imprint","IMPRINT",EDGE,{"disambiguationData":[TD([[subQ7,-1.0]])],"derivedFrom":subQ4}),1.0]])]});}
            extrude(context, id + "F20", {"entities" : qUnion([Q0]), "operationType" : NewBodyOperationType.ADD, "depth" : 7.62 * mm, "offsetDistance" : 25.4 * mm});
        }
        {
            var Q0;
            {var subQ0=sQuery(id+"F19.wireOp",EDGE,"E40");var subQ1=sQuery(id+"F19.wireOp",EDGE,"E38");var subQ2=makeQuery(id+"F19.imprint","INTERSECT",VERTEX,{"disambiguationData":[OD(0.0)],"derivedFrom":[subQ1,subQ0]});Q0=makeQuery(id+"F19.imprint","IMPRINT",FACE,{"disambiguationData":[TD([[makeQuery(id+"F19.imprint","IMPRINT",EDGE,{"disambiguationData":[TD([[subQ2,1.0]])],"derivedFrom":subQ1}),1.0]])]});}
            var Q1;
            {var subQ0=sQuery(id+"F19.wireOp",EDGE,"E39");var subQ1=sQuery(id+"F19.wireOp",EDGE,"E38");var subQ2=makeQuery(id+"F19.imprint","INTERSECT",VERTEX,{"disambiguationData":[OD(0.0)],"derivedFrom":[subQ1,subQ0]});Q1=makeQuery(id+"F19.imprint","IMPRINT",FACE,{"disambiguationData":[TD([[makeQuery(id+"F19.imprint","IMPRINT",EDGE,{"disambiguationData":[TD([[subQ2,-1.0]])],"derivedFrom":subQ1}),1.0]])]});}
            extrude(context, id + "F21", {"entities" : qUnion([Q0, Q1]), "operationType" : NewBodyOperationType.ADD, "depth" : 8.9 * mm, "offsetDistance" : 25.4 * mm});
        }
        {
            var Q0;
            {var subQ0=sQuery(id+"F19.wireOp",EDGE,"E43");Q0=makeQuery(id+"F19.imprint","IMPRINT",FACE,{"disambiguationData":[TD([[makeQuery(id+"F19.imprint","IMPRINT",EDGE,{"derivedFrom":subQ0}),-1.0]])]});}
            var Q1;
            {var subQ0=sQuery(id+"F19.wireOp",EDGE,"E41");Q1=makeQuery(id+"F19.imprint","IMPRINT",FACE,{"disambiguationData":[TD([[makeQuery(id+"F19.imprint","IMPRINT",EDGE,{"derivedFrom":subQ0}),1.0]])]});}
            extrude(context, id + "F22", {"entities" : qUnion([Q0, Q1]), "operationType" : NewBodyOperationType.ADD, "depth" : 8.25 * mm, "offsetDistance" : 25.4 * mm});
        }
        {
            var Q0;
            {var subQ1=sQuery(id+"F19.wireOp",EDGE,"E38");var subQ7=sQuery(id+"F19.wireOp",EDGE,"E42");var subQ8=makeQuery(id+"F19.imprint","INTERSECT",VERTEX,{"disambiguationData":[OD(0.0)],"derivedFrom":[subQ1,subQ7]});Q0=makeQuery(id+"F19.imprint","IMPRINT",FACE,{"disambiguationData":[TD([[makeQuery(id+"F19.imprint","IMPRINT",EDGE,{"disambiguationData":[TD([[subQ8,-1.0]])],"derivedFrom":subQ1}),-1.0]])]});}
            extrude(context, id + "F23", {"entities" : qUnion([Q0]), "operationType" : NewBodyOperationType.ADD, "depth" : 10.16 * mm, "offsetDistance" : 25.4 * mm});
        }
        {
            var Q0;
            {var subQ0=sQuery(id+"F19.wireOp",EDGE,"E42");var subQ1=sQuery(id+"F19.wireOp",EDGE,"E38");var subQ2=makeQuery(id+"F19.imprint","INTERSECT",VERTEX,{"disambiguationData":[OD(0.0)],"derivedFrom":[subQ1,subQ0]});Q0=makeQuery(id+"F19.imprint","IMPRINT",FACE,{"disambiguationData":[TD([[makeQuery(id+"F19.imprint","IMPRINT",EDGE,{"disambiguationData":[TD([[subQ2,1.0]])],"derivedFrom":subQ1}),1.0]])]});}
            var Q1;
            {var subQ0=sQuery(id+"F19.wireOp",EDGE,"E45");Q1=makeQuery(id+"F19.imprint","IMPRINT",FACE,{"disambiguationData":[TD([[makeQuery(id+"F19.imprint","IMPRINT",EDGE,{"derivedFrom":subQ0}),1.0]])]});}
            extrude(context, id + "F24", {"entities" : qUnion([Q0, Q1]), "operationType" : NewBodyOperationType.ADD, "depth" : 8.9 * mm, "offsetDistance" : 25.4 * mm});
        }
        {
            var Q0;
            Q0=qCreatedBy(makeId("Top.planeOp"),FACE);
            var sketch = newSketch(context, id + "F25", { "sketchPlane" : qUnion([Q0])});
            skFitSpline(sketch, "E46", {"points": [v(41.98, -153.77) * mm, v(44.5, -170.41) * mm, v(37.44, -205.71) * mm, v(12.22, -230.92) * mm, v(-10.47, -249.58) * mm, v(-18.54, -277.32) * mm, v(-9.96, -316.15) * mm, v(21.3, -342.87) * mm, v(36.3, -363.1) * mm, v(27.81, -372.44) * mm, v(38.84, -370.74) * mm, v(54.95, -358.02) * mm, v(50.7, -334.27) * mm, v(32.9, -313.92) * mm, v(11.7, -282.54) * mm, v(27.81, -247.77) * mm, v(36.3, -250.31) * mm, v(28.66, -274.06) * mm, v(37.99, -268.12) * mm, v(57.5, -252.86) * mm, v(69.37, -220.63) * mm, v(67.67, -190.1) * mm, v(54.1, -164.66) * mm, v(41.98, -153.77) * mm]});
            skSolve(sketch);
        }
        {
            var Q0;
            Q0 = qSketchRegion(id + "F25", true);
            extrude(context, id + "F26", {"entities" : qUnion([Q0]), "operationType" : NewBodyOperationType.ADD, "depth" : 10.16 * mm, "offsetDistance" : 25.4 * mm});
        }
        {
            var Q0;
            Q0=makeQuery(id+"F2.opExtrude","CAP_FACE",FACE,{"disambiguationData":[OSD([sQuery(id+"F0.wireOp",EDGE,"E2"),sQuery(id+"F0.wireOp",EDGE,"E3")])],"isStart":false});
            var sketch = newSketch(context, id + "F27", { "sketchPlane" : qUnion([Q0])});
            skFitSpline(sketch, "E47", {"points": [v(4.38, 15.9) * mm, v(6.04, 14.84) * mm, v(9.84, 14.84) * mm, v(14.42, 17.76) * mm, v(18.5, 16.88) * mm, v(16.76, 18.15) * mm, v(13.93, 19.9) * mm, v(10.81, 20.3) * mm, v(5.75, 18.35) * mm, v(4.38, 15.9) * mm]});
            skSolve(sketch);
        }
        {
            var Q0;
            Q0 = qSketchRegion(id + "F27", true);
            extrude(context, id + "F28", {"entities" : qUnion([Q0]), "operationType" : NewBodyOperationType.ADD, "depth" : 2.54 * mm, "offsetDistance" : 25.4 * mm});
        }
    });
